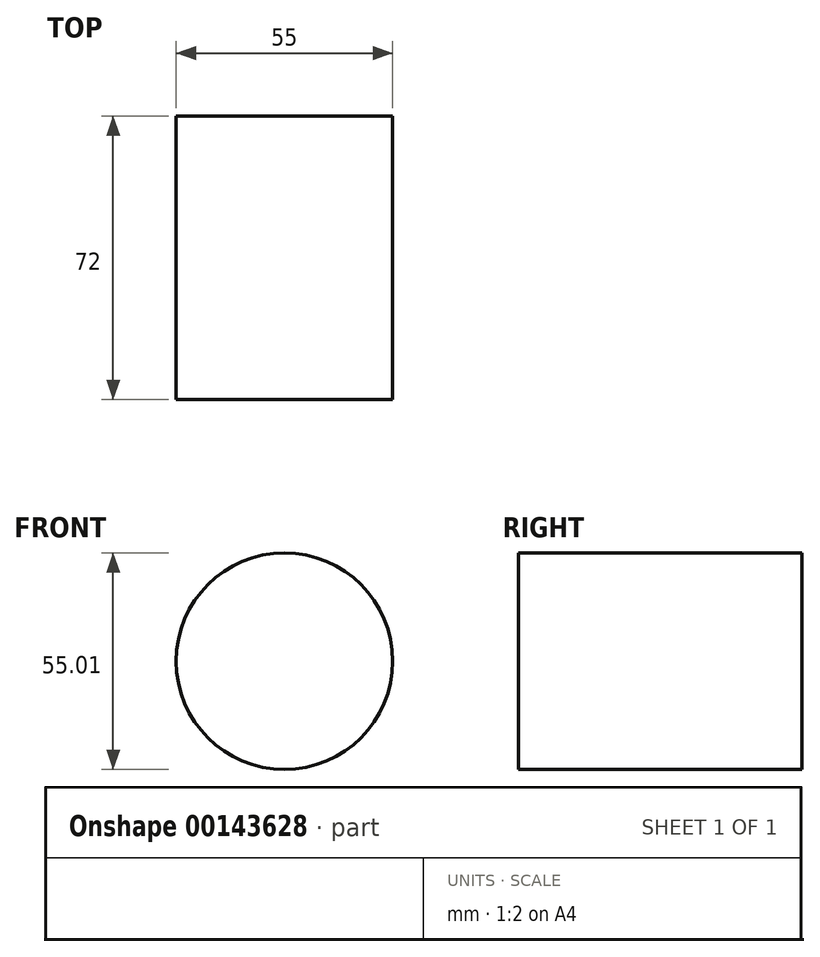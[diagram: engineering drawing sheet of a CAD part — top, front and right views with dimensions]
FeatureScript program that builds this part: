
annotation { "Feature Type Name" : "Feature", "Feature Type Description" : "" }
export const myFeature = defineFeature(function(context is Context, id is Id, definition is map)
    precondition{}
    {
        {
            var Q0;
            Q0=qCreatedBy(makeId("Front.planeOp"),FACE);
            var sketch = newSketch(context, id + "F1", { "sketchPlane" : qUnion([Q0])});
            skCircle(sketch, "E0", {"center": v(0, 6.3) * mm, "radius": 27.5 * mm});
            skSolve(sketch);
        }
        {
            var Q0;
            Q0=makeQuery(id+"F1.imprint","IMPRINT",FACE,{"disambiguationData":[TD([[makeQuery(id+"F1.imprint","IMPRINT",EDGE,{"derivedFrom":sQuery(id+"F1.wireOp",EDGE,"E0")}),1.0]])]});
            extrude(context, id + "F0", {"entities" : qUnion([Q0]), "depth" : 72 * mm});
        }
    });
